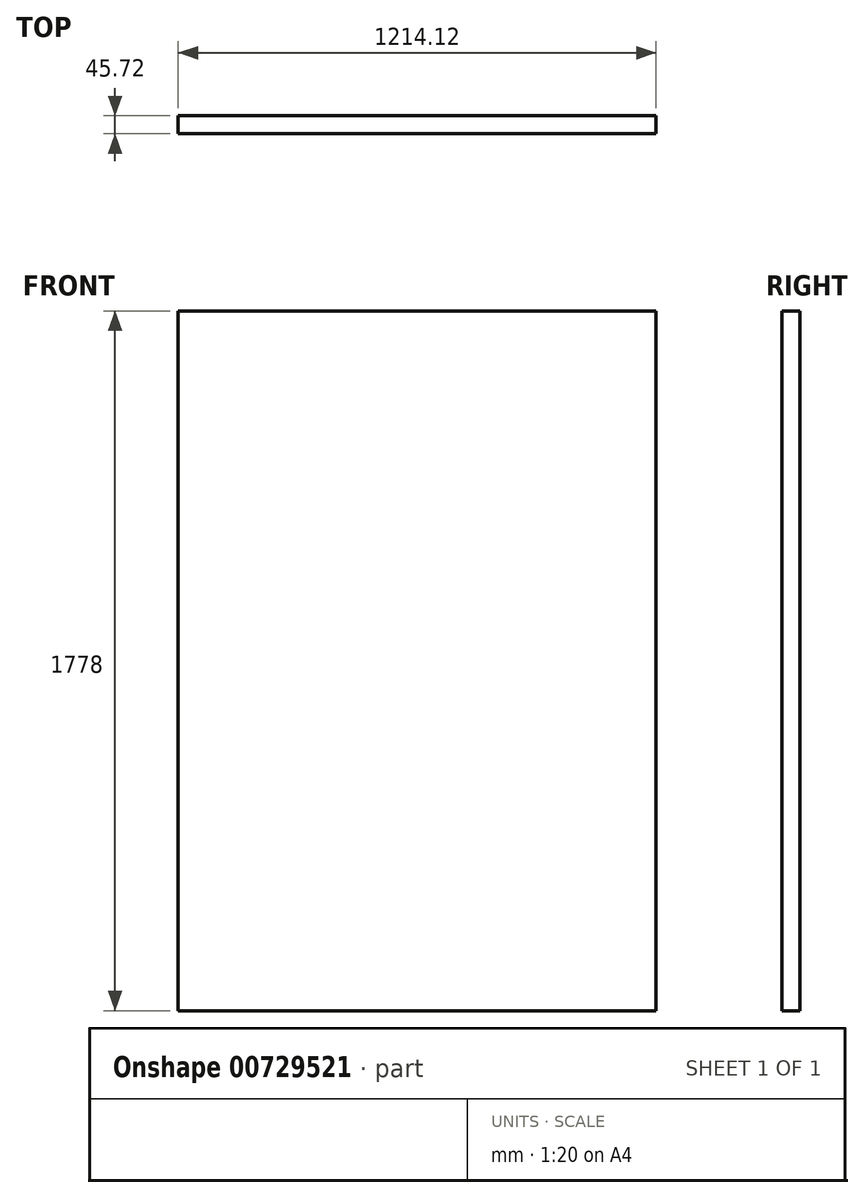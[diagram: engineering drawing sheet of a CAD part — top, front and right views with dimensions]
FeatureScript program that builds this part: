
annotation { "Feature Type Name" : "Feature", "Feature Type Description" : "" }
export const myFeature = defineFeature(function(context is Context, id is Id, definition is map)
    precondition{}
    {
        {
            var Q0;
            Q0=qCreatedBy(makeId("Front.planeOp"),FACE);
            var sketch = newSketch(context, id + "F0", { "sketchPlane" : qUnion([Q0])});
            skLineSegment(sketch, "E0.bottom", {"start": v(-105, 1655.47) * mm, "end": v(1109.12, 1655.47) * mm});
            skLineSegment(sketch, "E0.top", {"start": v(-105, -122.53) * mm, "end": v(1109.12, -122.53) * mm});
            skLineSegment(sketch, "E0.left", {"start": v(-105, 1655.47) * mm, "end": v(-105, -122.53) * mm});
            skLineSegment(sketch, "E0.right", {"start": v(1109.12, 1655.47) * mm, "end": v(1109.12, -122.53) * mm});
            skSolve(sketch);
        }
        {
            var Q0;
            Q0 = qSketchRegion(id + "F0", true);
            extrude(context, id + "F1", {"entities" : qUnion([Q0]), "depth" : 45.72 * mm, "offsetDistance" : 25.4 * mm});
        }
    });
